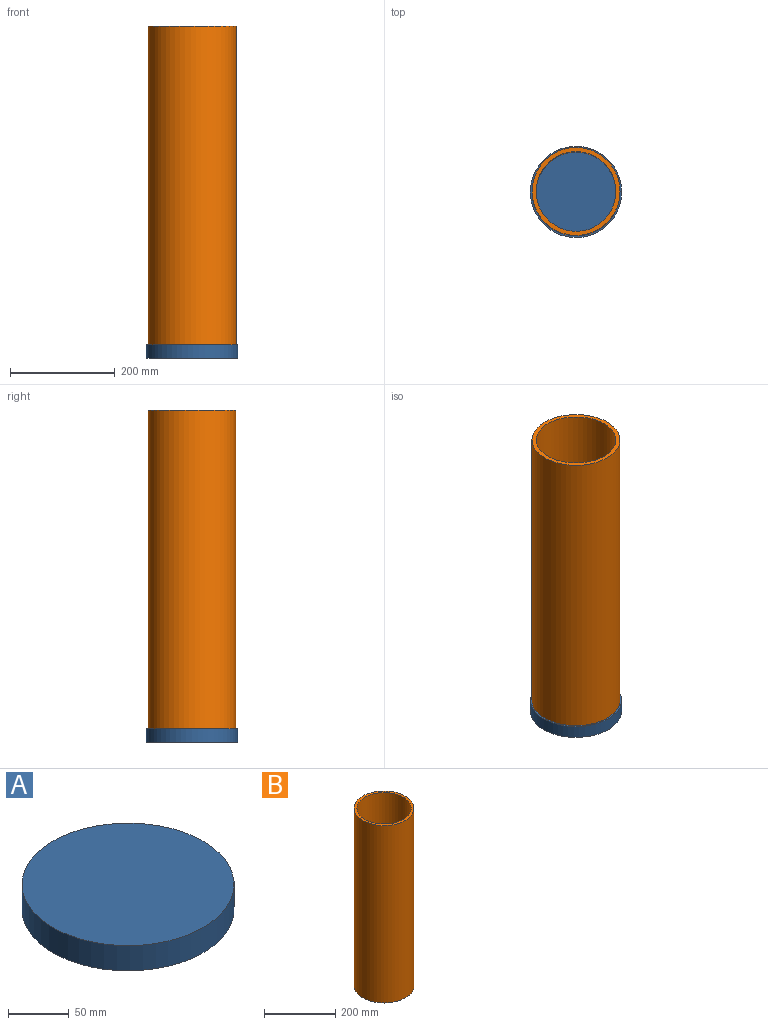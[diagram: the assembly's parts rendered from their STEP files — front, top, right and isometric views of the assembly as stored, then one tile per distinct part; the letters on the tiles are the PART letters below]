
ASSEMBLY  parts=2 mates=1
PART A: 5 faces, bbox 174.5x174.5x25.4 mm
  f0: cylinder r=87.27mm len=174.55mm, axis (0,0,-1), area 13928.3mm2, adj f1,f2
  f1: plane 174.55x174.55mm, normal (0,0,1), area 23928.8mm2, adj f0
  f2: plane 174.55x174.55mm, normal (0,0,-1), area 4008.6mm2, adj f0,f3
  f3: cylinder r=79.63mm len=159.26mm, axis (0,0,1), area 10166.6mm2, adj f2,f4
  f4: plane 159.26x159.26mm, normal (0,0,-1), area 19920.1mm2, adj f3
PART B: 4 faces, bbox 168.3x168.3x609.6 mm
  f0: cylinder r=76.2mm len=609.6mm, axis (0,0,-1), area 291863.5mm2, adj f2,f3
  f1: cylinder r=84.14mm len=609.6mm, axis (0,0,-1), area 322266mm2, adj f2,f3
  f2: plane 168.28x168.28mm, normal (0,0,1), area 3998.2mm2, adj f0,f1
  f3: plane 168.28x168.28mm, normal (0,0,-1), area 3998.2mm2, adj f0,f1
PLACE A rot(axis=(0,1,0),180deg) t=(230.68,-457.51,-190.62)mm
PLACE B t=(230.68,-457.51,-190.62)mm
MATE fastened B.f0 <-> A.f3  axis (0,0,-1) through (230.68,-457.51,-190.62)mm
